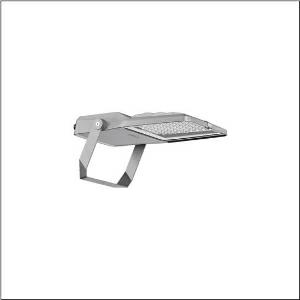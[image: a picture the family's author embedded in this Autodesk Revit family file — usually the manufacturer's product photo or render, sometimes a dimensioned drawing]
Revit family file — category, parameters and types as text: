
# Revit family: floodlight_fl_21_mini___pl52_5xa7776c2d1a_43f3
name_source: partatom
category: Lighting Fixtures
units: mm (PartAtom-declared; Revit-internal decimal feet)

## family parameters
Cut with Voids When Loaded = No
Host = Face
Light Source = No
Part Type = Normal
Room Calculation Point = No
Round Connector Dimension = Use Diameter
Shared = No

## types (1)
- --- (1 x LED, 12190 lm, 89 W, 3000K)
    Apparent Load = 89 VA
    CIE Flux Codes = 26 60 98 100 100
    Color Rendering = 70
    Color Temperature = 3000K
    Default Elevation = 1800 mm
    Description = Floodlight FL 21 mini, floodlight, primary light control with lens, of PMMA, primary optical cover: protective disc, of toughened safety glass, transparent, light distribution: PL52, light emission: direct distribution, installation type: surface-mounted, LED, High Power LED, rated luminous flux: 12.190lm, luminous efficacy: 137lm/W, light colour: 730, colour temperature: 3000K, control gear: Smart Interface (Zhaga), control: flexible luminous flux parameterisation, time-dependent luminous flux control, constant luminous flux control, overheat protection, pre-setting: logarithmic dimming characteristic, with terminal, 6-pole, mains connection: 220..240V, AC, 50/60Hz, start of lifetime: 89W, end of service life: 94W, reduction: 43W, luminaire housing, of diecast aluminium, powder-coated, SITECO metallic grey (DB 702S), corrosivity category C5 mid according to DIN EN ISO 12944, suitable for swimming pools, chlorine-resistant, sealing non-destructively replaceable, mounting bracket, of steel, galvanised, powder-coated, SITECO metallic grey (DB 702S), Smart Interface below and above, protection rating (complete): IP66, insulation class (complete): insulation class II (safety insulation), certification: CE, ENEC, VDE, protection symbol: D, impact resistance: IK08, permissible operating ambient temperature: -40..+40°C, permissible operating ambient temperature for outdoor applications: -40..+50°C, standard: DIN EN 12944, LABS conformity tested according to VDMA 24364:2018-05, packaging unit: 1 piece

Light Distribution: PL52
    Height = 70 mm
    Lamp = 1 x LED
    Lamp Light Flux = 12190 lm
    Lamp Power = 89 W
    Lamp count = 1
    Length = 485 mm
    Luminous efficacy = 137 lm/W
    Manufacturer = Siteco
    ModVariant = No
    Model = 5XA7776C2D1A
    Number of Poles = 1
    OnlyDefault = Yes
    Power Factor = 1
    Product Name = Floodlight FL 21 mini | PL52
    Product group = floodlight | pylon annexe
    ProductGroupID = 6201
    Protection Class = Protection class II
    Protection Degree = IP 66
    RLX_Detail_Level = 1
    RLX_Emergency_Light_Flux = 0 lm
    RLX_Emergency_Type = 0
    RLX_Emergency_Type_DB = No
    RlxData = <blob elided: 96125 chars, md5=9bf24f2f>
    Socket = socket
    Standby Power = 0 W
    System Light Flux = 12190 lm
    System Power = 89 W
    Type Comments = factory setting: luminous flux: 100 % | dim-lin: 254 | 456 mA
    Type Image = l_1006845.jpg
    URL = http://relux.com
    VarID = @adj_162753
    Voltage = 0 V
    Weight = 0.00 kg
    Width = 337 mm

## geometry (parser evidence)
native form markers: Blend x4, Sweep x13
no freeform markers — native parametric forms only
